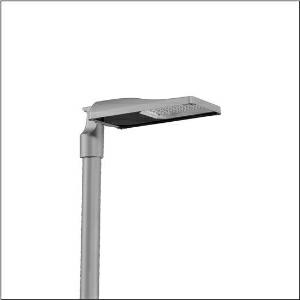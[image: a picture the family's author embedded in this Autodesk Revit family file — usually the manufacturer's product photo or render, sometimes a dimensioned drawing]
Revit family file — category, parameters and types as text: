
# Revit family: streetlight_sl_31_mini___st1_0a_5xh2d3aa08ga_e7bb
name_source: partatom
category: Lighting Fixtures
units: mm (PartAtom-declared; Revit-internal decimal feet)

## family parameters
Cut with Voids When Loaded = No
Host = Face
Light Source = No
Part Type = Normal
Room Calculation Point = No
Round Connector Dimension = Use Diameter
Shared = No

## types (1)
- --- (1 x LED, 5710 lm, 37.3 W, 3000K)
    Apparent Load = 37 VA
    CIE Flux Codes = 37 72 97 100 100
    Color Rendering = 70
    Color Temperature = 3000K
    Default Elevation = 1800 mm
    Description = Streetlight SL 31 mini Easy mast luminaire for post-top, side-entry; light control with lens of PMMA; light distribution: ST1.0a, direct asymmetric distribution, for standard-compliant lighting for roads and squares; LED: luminous flux: 5.710lm, light colour: 730, colour temperature: 3000K; luminous efficacy: 153,1lm/W; control: overheat protection, intelligent temperature release in ECG and LED module, constant luminous flux control, time-dependent luminous flux control, flexible luminous flux parameterisation, pre-setting: linear dimming characteristic; luminaire housing, of diecast aluminium, Siteco® metallic grey (DB 702S), corrosivity category C5 high according to DIN EN ISO 12944; cover of toughened safety glass, transparent, mast flange of diecast aluminium, Siteco® metallic grey (DB 702S), spigot size: 76/60mm, mast flange included unmounted; with cable H07RN-F 2x 1.5mm², cable length: 6,5m, connection cable pre-assembled; mains connection: 220..240V, AC, 50/60Hz; power consumption (at start of service life): 37,3W / (at end of service life): 38,7W / (with reduced operation 50%): 17,5W; protection rating (complete): IP66; insulation class (complete): insulation class II (safety insulation); impact resistance: IK10; certification: CE, ENEC, ENEC+, VDE, UKCA; permissible operating ambient temperature for outdoor applications: -40..+50°C; packaging unit: 1 piece

Light Distribution: ST1.0a
    Height = 76 mm
    Lamp = 1 x LED
    Lamp Light Flux = 5710 lm
    Lamp Power = 37.3 W
    Lamp count = 1
    Length = 547 mm
    Luminous efficacy = 153 lm/W
    Manufacturer = Siteco
    ModVariant = No
    Model = 5XH2D3AA08GA
    Number of Poles = 1
    OnlyDefault = Yes
    Power Factor = 1
    Product Name = Streetlight SL 31 mini | ST1.0a
    Product group = mast luminaire | pylon top
    ProductGroupID = 6100
    Protection Class = Protection class II
    Protection Degree = IP 66
    RLX_Detail_Level = 1
    RLX_Emergency_Light_Flux = 0 lm
    RLX_Emergency_Type = 0
    RLX_Emergency_Type_DB = No
    RlxData = <blob elided: 39421 chars, md5=39f12ffa>
    Socket = socket
    Standby Power = 0 W
    System Light Flux = 5710 lm
    System Power = 37 W
    Type Comments = factory setting: luminous flux: 100 % | dim-lin: 254 | 386 mA
    Type Image = l_1300326.jpg
    URL = http://relux.com
    VarID = @adj_075527
    Voltage = 0 V
    Weight = 0.00 kg
    Width = 265 mm

## geometry (parser evidence)
native form markers: Blend x4, Sweep x9
no freeform markers — native parametric forms only
